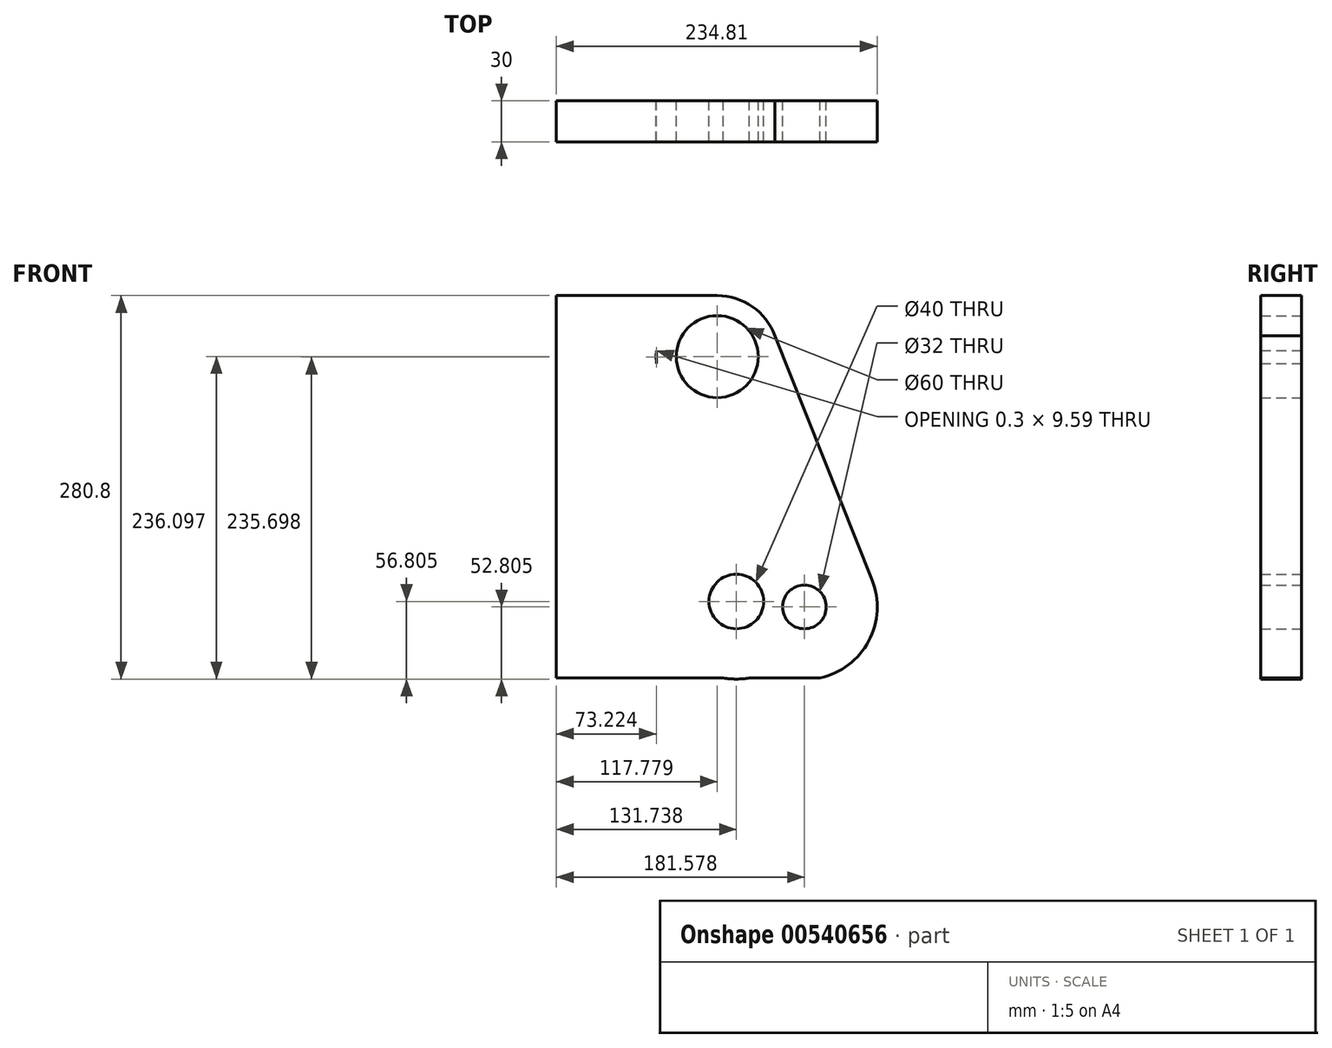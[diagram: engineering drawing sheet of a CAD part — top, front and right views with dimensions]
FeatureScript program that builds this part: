
annotation { "Feature Type Name" : "Feature", "Feature Type Description" : "" }
export const myFeature = defineFeature(function(context is Context, id is Id, definition is map)
    precondition{}
    {
        {
            var Q0;
            Q0=qCreatedBy(makeId("Front.planeOp"),FACE);
            var sketch = newSketch(context, id + "F0", { "sketchPlane" : qUnion([Q0])});
            skLineSegment(sketch, "E0", {"start": v(-60.6, 216.5) * mm, "end": v(-60.6, -63.5) * mm});
            skLineSegment(sketch, "E1", {"start": v(-60.6, 216.5) * mm, "end": v(57.18, 216.5) * mm});
            skLineSegment(sketch, "E2", {"start": v(-60.6, -63.5) * mm, "end": v(7.52, -63.5) * mm});
            skPoint(sketch, "E3.visualSharp", {"position": v(-14.68, 179.06) * mm});
            skPoint(sketch, "E4.start.orphan", {"position": v(58.18, -63.5) * mm});
            skLineSegment(sketch, "E5", {"start": v(7.52, -63.5) * mm, "end": v(58.18, -63.5) * mm});
            skArc(sketch, "E6", {"start": v(99.26, 186.9) * mm, "mid": v(46.96, 215.31) * mm, "end": v(12.77, 166.6) * mm});
            skArc(sketch, "E7", {"start": v(14.34, -8.01) * mm, "mid": v(34.68, -51.06) * mm, "end": v(80.64, -63.5) * mm});
            skArc(sketch, "E8", {"start": v(132.38, -63.5) * mm, "mid": v(168, -36.46) * mm, "end": v(170.43, 8.2) * mm});
            skLineSegment(sketch, "E9", {"start": v(12.69, 176.18) * mm, "end": v(14.34, -8.01) * mm});
            skLineSegment(sketch, "E10", {"start": v(58.18, -63.5) * mm, "end": v(132.38, -63.5) * mm});
            skLineSegment(sketch, "E11", {"start": v(98.65, 188.5) * mm, "end": v(99.26, 186.9) * mm});
            skCircle(sketch, "E12", {"center": v(57.18, 171.79) * mm, "radius": 30 * mm});
            skCircle(sketch, "E13", {"center": v(57.18, 171.79) * mm, "radius": 16 * mm});
            skCircle(sketch, "E14", {"center": v(71.14, -7.5) * mm, "radius": 20 * mm});
            skCircle(sketch, "E15", {"center": v(71.14, -7.5) * mm, "radius": 10 * mm});
            skCircle(sketch, "E16", {"center": v(120.98, -11.5) * mm, "radius": 16 * mm});
            skPoint(sketch, "E17.orphan", {"position": v(58.18, 216.5) * mm});
            skLineSegment(sketch, "E18", {"start": v(99.26, 186.9) * mm, "end": v(170.43, 8.2) * mm});
            skSolve(sketch);
        }
        {
            var Q0;
            Q0 = qSketchRegion(id + "F0", true);
            extrude(context, id + "F1", {"entities" : qUnion([Q0]), "depth" : 30 * mm, "offsetDistance" : 25 * mm});
        }
    });
